# Revit family: LUXI_DOWNLIGHT_CC
name_source: partatom
category: Apparecchi per illuminazione
revit_build: Autodesk Revit 2016 (Build: 20161004_0715(x64)
units: mm (PartAtom-declared; Revit-internal decimal feet)

## family parameters
Condiviso = No
Host = Superficie
Numero OmniClass = 23.80.70.00
Punto di calcolo locali = Sì
Quota connettore circolare = Usa diametro
Sorgente d'illuminazione = Sì
Taglio con vuoti quando caricato = No
Tipo di parte = Normale
Titolo OmniClass = Lighting

## types (3) — shared parameters
Angolo inclinazione = -90.00°
Certifications = CE / RohS
Color = White (frame)
Descrizione = LED Downlight
Dimming = 1-10V / DALI / PUSH DIM (optional)
Dust and water protection rating = IP 20
Energy class = A+
Filtro dei colori = 16777215
IFCExportAs = IfcLightFixtureType
Impact rating = IK06 (1 Joule)
Installation = Recessed
Lifetime = L70B20 50.000h
Light distribution = Edge light
Light source = LED SMD
Masterformat 2016 code = 26.50.00
Masterformat 2016 description = Lighting
Material 1 = Polycarbonate_White
Material 2 = Opal Technopolimer
Material 3 = Molded Aluminum_Grey
Modello = CC Series | Downlight
Operating temperature = 0°C / +40°C
Optics = Metalized reflector UGR≤19
Photobiological risk group = RG0
Power factor = ≥0,95 (typ.)
Power supply = Included, not dimmable
Produttore = Luxi Illuminazione S.r.l.
Prospetto di default = 2000 mm  [stored 6.56168 ft]
Protection class = II
Rated supply voltage = 220-240V AC / 50-60 Hz
Rendi la forma visibile nel rendering = No
Review = 3
Step MacAdam (SDCM) = <3
URL = https://www.luxi.lighting
Uniclass 2015 code = EF_70_80
Uniclass 2015 description = Lighting
Variazione temperatura colore lampada con luminosità attenuata = <Nessuno>
Warranty = 5 years

## per-type parameters (varying)
| type | CRI | Carico apparente | Diameter | Emetti da diametro cerchio | File diagramma fotometrico | H | OFF1 | OFF2 | OFF3 | Recession | Size | Wattage | Weight |
| DLCC012120WX840 | ≥80 (typ.) | 12 VA | 140 mm  [stored 0.459318 ft] | 105 mm | DLCC012120WX840 Luxi Serie CC 12W 4000K UGR19.IES | 68 mm | 41 mm | 45 mm  [stored 0.147638 ft] | 54 mm  [stored 0.177165 ft] | 120 mm  [stored 0.393701 ft] | Ø140x68 recession Ø120 | 12 W | 0.32 kg |
| DLCC022150WX940 | ≥90 (typ.) | 22 VA | 180 mm  [stored 0.590551 ft] | 145 mm | DLCC022150WX840 Luxi Serie CC 22W 4000K UGR19.IES | 90 mm  [stored 0.295276 ft] | 63 mm | 60 mm  [stored 0.19685 ft] | 69 mm  [stored 0.226378 ft] | 150 mm | Ø180x90 recession Ø150 | 22 W | 0.52 kg |
| DLCC032200WX840 | ≥80 (typ.) | 32 VA | 230 mm  [stored 0.754593 ft] | 195 mm | DLCC032200WX840 Luxi Serie CC 32W 4000K UGR19.IES | 120 mm  [stored 0.393701 ft] | 93 mm | 85 mm  [stored 0.278871 ft] | 94 mm  [stored 0.308399 ft] | 200 mm  [stored 0.656168 ft] | Ø230x120 recession Ø200 | 32 W | 0.92 kg |

note: column(s) folded — value = type name in every type: Code

note: [stored X ft] marks values corroborated as IEEE doubles in the binary element streams (Revit-internal decimal feet)
